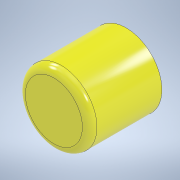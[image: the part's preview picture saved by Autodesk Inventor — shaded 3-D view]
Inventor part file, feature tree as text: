
AUTODESK INVENTOR PART (.ipt)
format: ipt  version: 2022.1 (Build 261234000, 234)  size: 120,832 bytes
history: native  units: in
note: dims shown in document units (in); Inventor stores cm internally (conversion verified against a paired STEP export)
features: extrude x1, fillet x1, sketch x1
ambient origin geometry x8: Origin, YZ Plane, XZ Plane, XY Plane, X Axis, Y Axis, Z Axis, Center Point
bodies: Solid1 (feature_tree)
feature tree (3):
  extrude  "Extrusion1"  Depth=0.1986in TaperAngle=0.0deg
  fillet  "Face Fillet1"
  sketch  "Sketch1"  dims[d0=0.1969in d1=0.1986in d2=0.0in d3=0.02in]
